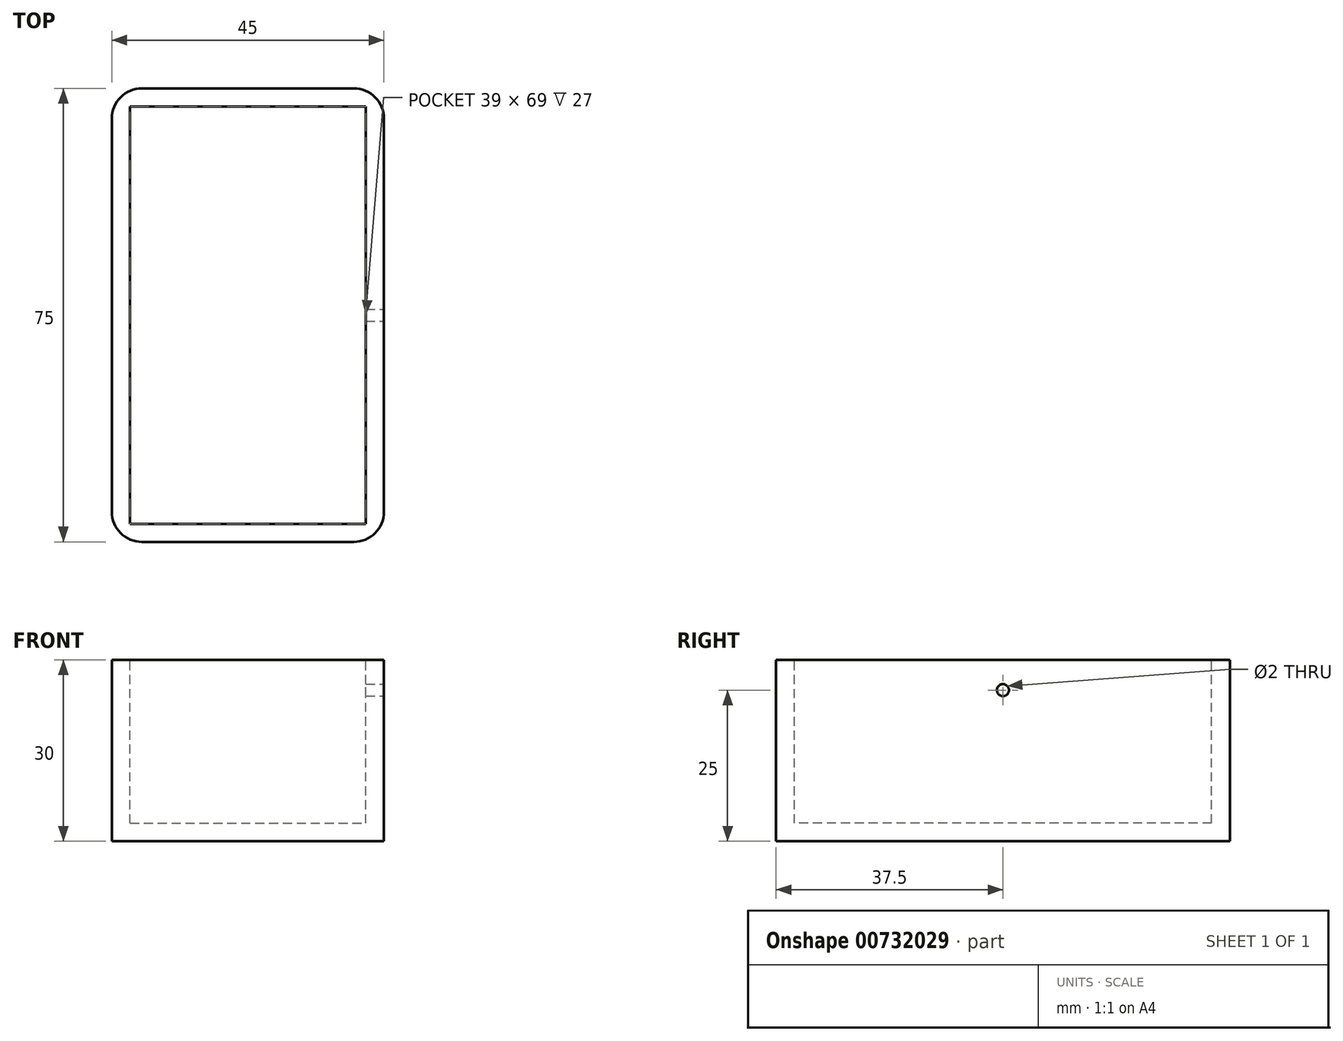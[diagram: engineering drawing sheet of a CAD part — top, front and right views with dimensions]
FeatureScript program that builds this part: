
annotation { "Feature Type Name" : "Feature", "Feature Type Description" : "" }
export const myFeature = defineFeature(function(context is Context, id is Id, definition is map)
    precondition{}
    {
        {
            var Q0;
            Q0=qCreatedBy(makeId("Top.planeOp"),FACE);
            var sketch = newSketch(context, id + "F0", { "sketchPlane" : qUnion([Q0])});
            skLineSegment(sketch, "E0.bottom", {"start": v(-22.5, 37.5) * mm, "end": v(22.5, 37.5) * mm});
            skLineSegment(sketch, "E0.top", {"start": v(-22.5, -37.5) * mm, "end": v(22.5, -37.5) * mm});
            skLineSegment(sketch, "E0.left", {"start": v(-22.5, 37.5) * mm, "end": v(-22.5, -37.5) * mm});
            skLineSegment(sketch, "E0.right", {"start": v(22.5, 37.5) * mm, "end": v(22.5, -37.5) * mm});
            skPoint(sketch, "E0.middle", {"position": v(0, 0) * mm});
            skSolve(sketch);
        }
        {
            var Q0;
            Q0 = qSketchRegion(id + "F0", true);
            extrude(context, id + "F1", {"entities" : qUnion([Q0]), "depth" : 30 * mm, "offsetDistance" : 25 * mm});
        }
        {
            var Q0;
            Q0=makeQuery(id+"F1.opExtrude","CAP_FACE",FACE,{"disambiguationData":[OSD([sQuery(id+"F0.wireOp",EDGE,"E0.bottom"),sQuery(id+"F0.wireOp",EDGE,"E0.top"),sQuery(id+"F0.wireOp",EDGE,"E0.left"),sQuery(id+"F0.wireOp",EDGE,"E0.right")])],"isStart":false});
            var sketch = newSketch(context, id + "F2", { "sketchPlane" : qUnion([Q0])});
            skLineSegment(sketch, "E1.bottom", {"start": v(-19.5, 34.5) * mm, "end": v(19.5, 34.5) * mm});
            skLineSegment(sketch, "E1.top", {"start": v(-19.5, -34.5) * mm, "end": v(19.5, -34.5) * mm});
            skLineSegment(sketch, "E1.left", {"start": v(-19.5, 34.5) * mm, "end": v(-19.5, -34.5) * mm});
            skLineSegment(sketch, "E1.right", {"start": v(19.5, 34.5) * mm, "end": v(19.5, -34.5) * mm});
            skPoint(sketch, "E1.middle", {"position": v(0, 0) * mm});
            skSolve(sketch);
        }
        {
            var Q0;
            Q0 = qSketchRegion(id + "F2", true);
            extrude(context, id + "F3", {"entities" : qUnion([Q0]), "operationType" : NewBodyOperationType.REMOVE, "oppositeDirection" : true, "depth" : 27 * mm, "offsetDistance" : 25 * mm});
        }
        {
            var Q0;
            Q0=makeQuery(id+"F1.opExtrude","SWEPT_EDGE",EDGE,{"disambiguationData":[OSD([sQuery(id+"F0.wireOp",EDGE,"E0.top"),sQuery(id+"F0.wireOp",EDGE,"E0.right")])]});
            var Q1;
            Q1=makeQuery(id+"F1.opExtrude","SWEPT_EDGE",EDGE,{"disambiguationData":[OSD([sQuery(id+"F0.wireOp",EDGE,"E0.top"),sQuery(id+"F0.wireOp",EDGE,"E0.left")])]});
            var Q2;
            Q2=makeQuery(id+"F1.opExtrude","SWEPT_EDGE",EDGE,{"disambiguationData":[OSD([sQuery(id+"F0.wireOp",EDGE,"E0.bottom"),sQuery(id+"F0.wireOp",EDGE,"E0.right")])]});
            var Q3;
            Q3=makeQuery(id+"F1.opExtrude","SWEPT_EDGE",EDGE,{"disambiguationData":[OSD([sQuery(id+"F0.wireOp",EDGE,"E0.bottom"),sQuery(id+"F0.wireOp",EDGE,"E0.left")])]});
            fillet(context, id + "F4", {"entities" : qUnion([Q0, Q1, Q2, Q3]), "radius" : 5 * mm, "tangentPropagation" : true, "allowEdgeOverflow" : false});
        }
        {
            var Q0;
            Q0=makeQuery(id+"F1.opExtrude","SWEPT_FACE",FACE,{"disambiguationData":[OSD([sQuery(id+"F0.wireOp",EDGE,"E0.right")])]});
            var sketch = newSketch(context, id + "F5", { "sketchPlane" : qUnion([Q0])});
            skCircle(sketch, "E2", {"center": v(0, 25) * mm, "radius": 1 * mm});
            skSolve(sketch);
        }
        {
            var Q0;
            Q0 = qSketchRegion(id + "F5", true);
            extrude(context, id + "F6", {"entities" : qUnion([Q0]), "operationType" : NewBodyOperationType.REMOVE, "oppositeDirection" : true, "depth" : 3 * mm, "offsetDistance" : 25 * mm});
        }
    });
